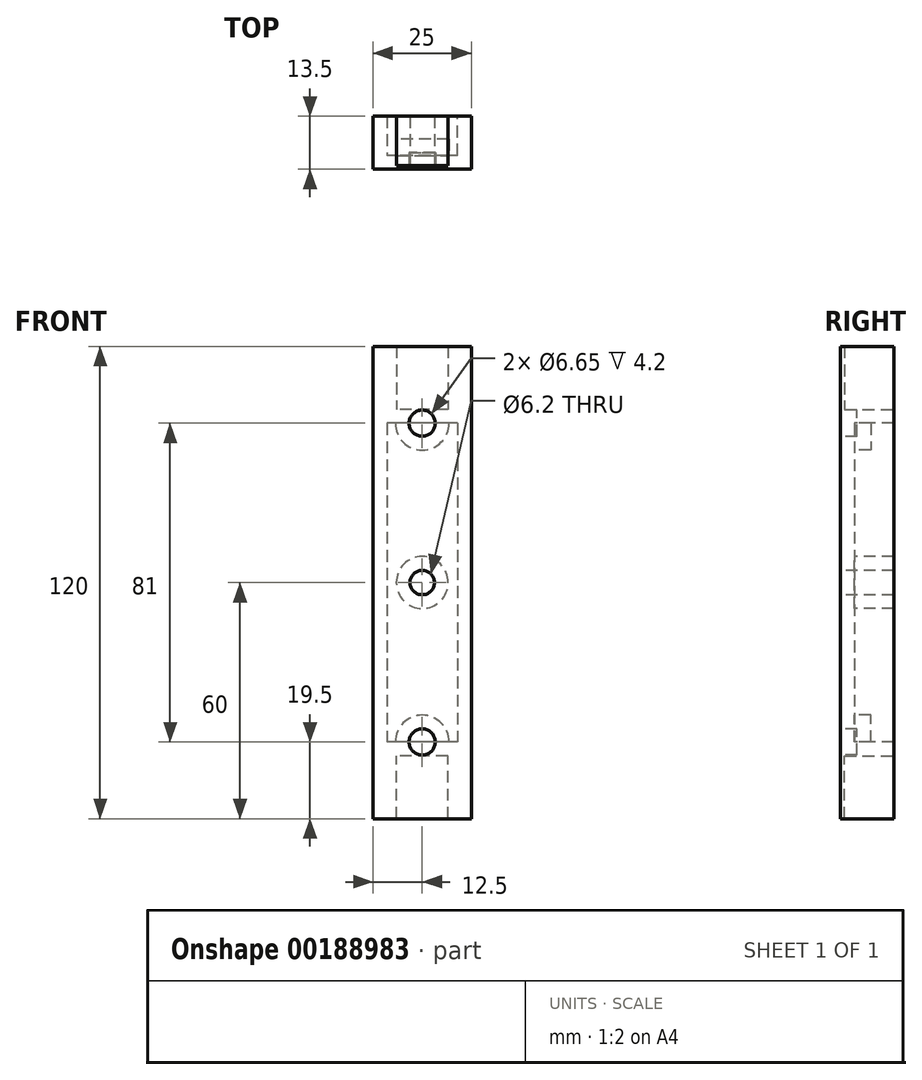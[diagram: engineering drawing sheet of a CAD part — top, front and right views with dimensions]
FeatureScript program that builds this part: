
annotation { "Feature Type Name" : "Feature", "Feature Type Description" : "" }
export const myFeature = defineFeature(function(context is Context, id is Id, definition is map)
    precondition{}
    {
        {
            var Q0;
            Q0=qCreatedBy(makeId("Front.planeOp"),FACE);
            var sketch = newSketch(context, id + "F0", { "sketchPlane" : qUnion([Q0])});
            skLineSegment(sketch, "E0.bottom", {"start": v(12.5, 60) * mm, "end": v(-12.5, 60) * mm});
            skLineSegment(sketch, "E0.top", {"start": v(12.5, -60) * mm, "end": v(-12.5, -60) * mm});
            skLineSegment(sketch, "E0.left", {"start": v(12.5, 60) * mm, "end": v(12.5, -60) * mm});
            skLineSegment(sketch, "E0.right", {"start": v(-12.5, 60) * mm, "end": v(-12.5, -60) * mm});
            skPoint(sketch, "E0.middle", {"position": v(0, 0) * mm});
            skSolve(sketch);
        }
        {
            var Q0;
            Q0 = qSketchRegion(id + "F0", true);
            extrude(context, id + "F1", {"entities" : qUnion([Q0]), "depth" : 13.5 * mm});
        }
        {
            var Q0;
            Q0=makeQuery(id+"F1.opExtrude","CAP_FACE",FACE,{"disambiguationData":[OSD([sQuery(id+"F0.wireOp",EDGE,"E0.bottom"),sQuery(id+"F0.wireOp",EDGE,"E0.top"),sQuery(id+"F0.wireOp",EDGE,"E0.left"),sQuery(id+"F0.wireOp",EDGE,"E0.right")])],"isStart":false});
            var sketch = newSketch(context, id + "F2", { "sketchPlane" : qUnion([Q0])});
            skCircle(sketch, "E1", {"center": v(0, 0) * mm, "radius": 3.1 * mm});
            skSolve(sketch);
        }
        {
            var Q0;
            Q0 = qSketchRegion(id + "F2", true);
            extrude(context, id + "F3", {"entities" : qUnion([Q0]), "operationType" : NewBodyOperationType.REMOVE, "endBound" : BoundingType.THROUGH_ALL, "oppositeDirection" : true, "depth" : 25 * mm});
        }
        {
            var Q0;
            Q0=makeQuery(id+"F1.opExtrude","CAP_FACE",FACE,{"disambiguationData":[OSD([sQuery(id+"F0.wireOp",EDGE,"E0.bottom"),sQuery(id+"F0.wireOp",EDGE,"E0.top"),sQuery(id+"F0.wireOp",EDGE,"E0.left"),sQuery(id+"F0.wireOp",EDGE,"E0.right")])],"isStart":true});
            var sketch = newSketch(context, id + "F4", { "sketchPlane" : qUnion([Q0])});
            skLineSegment(sketch, "E2.bottom", {"start": v(-6.5, 61.86) * mm, "end": v(6.5, 61.86) * mm});
            skLineSegment(sketch, "E2.top", {"start": v(-6.5, 44) * mm, "end": v(6.5, 44) * mm});
            skLineSegment(sketch, "E2.left", {"start": v(-6.5, 61.86) * mm, "end": v(-6.5, 44) * mm});
            skLineSegment(sketch, "E2.right", {"start": v(6.5, 61.86) * mm, "end": v(6.5, 44) * mm});
            skPoint(sketch, "E2.middle", {"position": v(0, 52.93) * mm});
            skLineSegment(sketch, "E3.MirrorCS", {"start": v(6.5, -61.86) * mm, "end": v(6.5, -44) * mm});
            skLineSegment(sketch, "E4.MirrorCS", {"start": v(-6.5, -61.86) * mm, "end": v(-6.5, -44) * mm});
            skLineSegment(sketch, "E5.MirrorCS", {"start": v(-6.5, -44) * mm, "end": v(6.5, -44) * mm});
            skLineSegment(sketch, "E6.MirrorCS", {"start": v(-6.5, -61.86) * mm, "end": v(6.5, -61.86) * mm});
            skPoint(sketch, "E7.MirrorP", {"position": v(0, -52.93) * mm});
            skSolve(sketch);
        }
        {
            var Q0;
            Q0 = qSketchRegion(id + "F4", true);
            extrude(context, id + "F5", {"entities" : qUnion([Q0]), "operationType" : NewBodyOperationType.REMOVE, "oppositeDirection" : true, "depth" : 12.5 * mm});
        }
        {
            var Q0;
            Q0=makeQuery(id+"F1.opExtrude","CAP_FACE",FACE,{"disambiguationData":[OSD([sQuery(id+"F0.wireOp",EDGE,"E0.bottom"),sQuery(id+"F0.wireOp",EDGE,"E0.top"),sQuery(id+"F0.wireOp",EDGE,"E0.left"),sQuery(id+"F0.wireOp",EDGE,"E0.right")])],"isStart":false});
            var sketch = newSketch(context, id + "F6", { "sketchPlane" : qUnion([Q0])});
            skCircle(sketch, "E8", {"center": v(0, -40.5) * mm, "radius": 3.33 * mm});
            skCircle(sketch, "E9.MirrorC", {"center": v(0, 40.5) * mm, "radius": 3.33 * mm});
            skSolve(sketch);
        }
        {
            var Q0;
            Q0 = qSketchRegion(id + "F6", true);
            extrude(context, id + "F7", {"entities" : qUnion([Q0]), "operationType" : NewBodyOperationType.REMOVE, "oppositeDirection" : true, "depth" : 4.2 * mm});
        }
        {
            var Q0;
            Q0=makeQuery(id+"F1.opExtrude","CAP_FACE",FACE,{"disambiguationData":[OSD([sQuery(id+"F0.wireOp",EDGE,"E0.bottom"),sQuery(id+"F0.wireOp",EDGE,"E0.top"),sQuery(id+"F0.wireOp",EDGE,"E0.left"),sQuery(id+"F0.wireOp",EDGE,"E0.right")])],"isStart":true});
            shell(context, id + "F8", {"entities" : qUnion([Q0]), "thickness" : 3.5 * mm});
        }
    });
